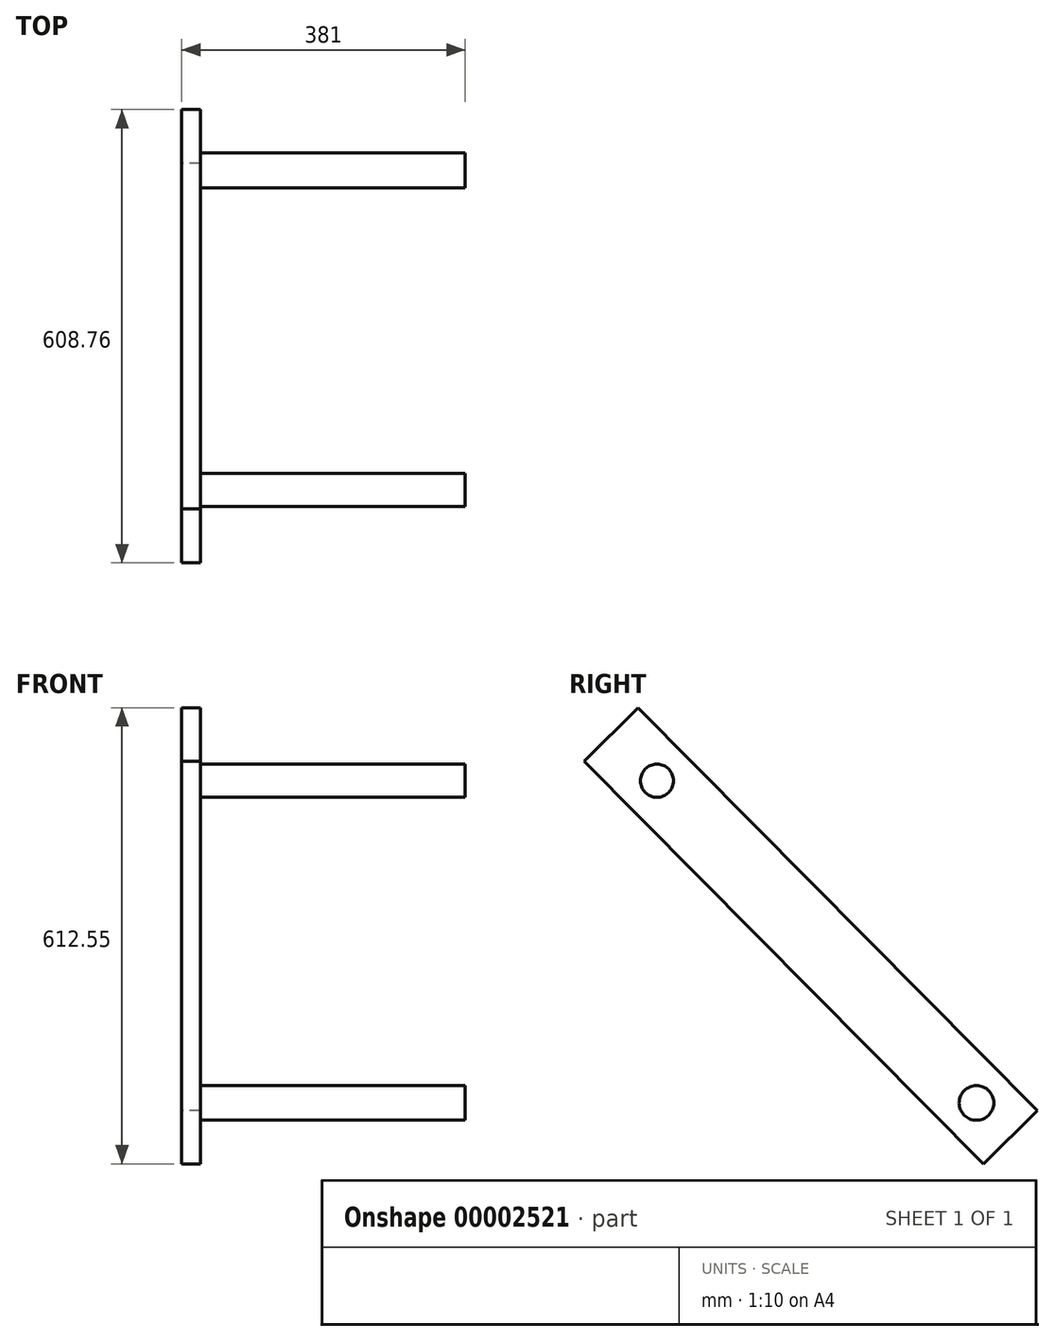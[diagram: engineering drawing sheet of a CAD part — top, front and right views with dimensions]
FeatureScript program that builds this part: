
annotation { "Feature Type Name" : "Feature", "Feature Type Description" : "" }
export const myFeature = defineFeature(function(context is Context, id is Id, definition is map)
    precondition{}
    {
        {
            var Q0;
            Q0=qCreatedBy(makeId("Right.planeOp"),FACE);
            var sketch = newSketch(context, id + "F0", { "sketchPlane" : qUnion([Q0])});
            skLineSegment(sketch, "E0", {"start": v(-66.13, 40.34) * mm, "end": v(470.5, -500.66) * mm});
            skLineSegment(sketch, "E1", {"start": v(470.5, -500.66) * mm, "end": v(542.63, -429.1) * mm});
            skLineSegment(sketch, "E2", {"start": v(542.63, -429.1) * mm, "end": v(6, 111.9) * mm});
            skLineSegment(sketch, "E3", {"start": v(6, 111.9) * mm, "end": v(-66.13, 40.34) * mm});
            skSolve(sketch);
        }
        {
            var Q0;
            Q0 = qSketchRegion(id + "F0", true);
            extrude(context, id + "F1", {"entities" : qUnion([Q0]), "depth" : 25.4 * mm});
        }
        {
            var Q0;
            Q0=makeQuery(id+"F1.opExtrude","CAP_FACE",FACE,{"disambiguationData":[OSD([sQuery(id+"F0.wireOp",EDGE,"E0"),sQuery(id+"F0.wireOp",EDGE,"E1"),sQuery(id+"F0.wireOp",EDGE,"E2"),sQuery(id+"F0.wireOp",EDGE,"E3")])],"isStart":false});
            var sketch = newSketch(context, id + "F2", { "sketchPlane" : qUnion([Q0])});
            skLineSegment(sketch, "E4", {"start": v(-30.06, 76.12) * mm, "end": v(506.56, -464.88) * mm, "construction": true});
            skCircle(sketch, "E5", {"center": v(31.62, 13.93) * mm, "radius": 22.23 * mm});
            skCircle(sketch, "E6", {"center": v(460.92, -418.87) * mm, "radius": 23.28 * mm});
            skSolve(sketch);
        }
        {
            var Q0;
            Q0 = qSketchRegion(id + "F2", true);
            extrude(context, id + "F3", {"entities" : qUnion([Q0]), "depth" : 355.6 * mm});
        }
    });
